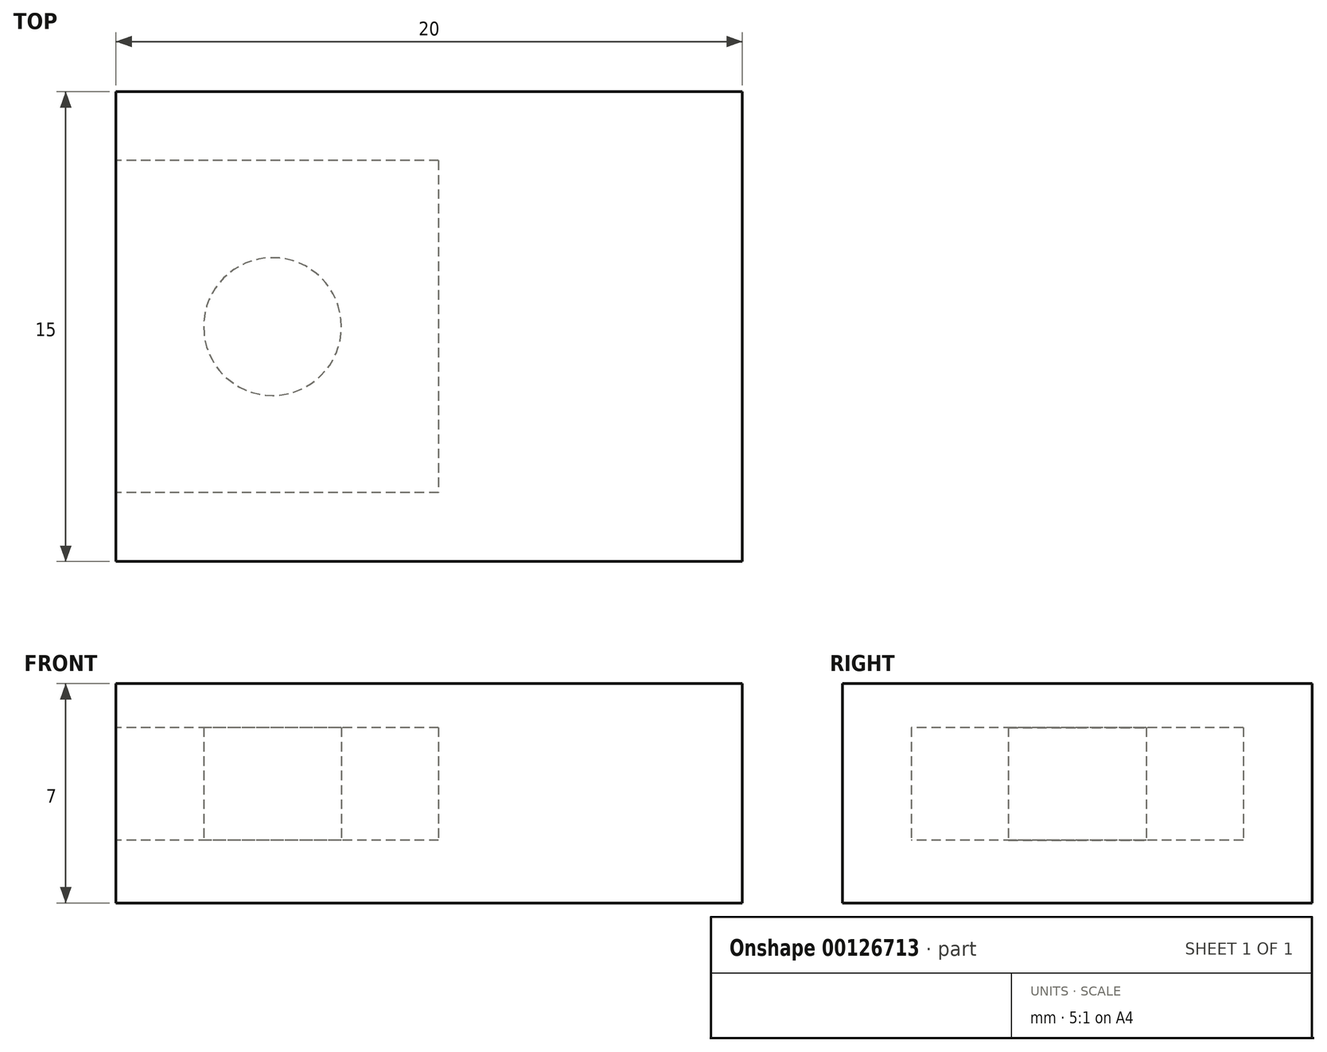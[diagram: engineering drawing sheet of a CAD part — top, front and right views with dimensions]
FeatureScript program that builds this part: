
annotation { "Feature Type Name" : "Feature", "Feature Type Description" : "" }
export const myFeature = defineFeature(function(context is Context, id is Id, definition is map)
    precondition{}
    {
        {
            var Q0;
            Q0=qCreatedBy(makeId("Top.planeOp"),FACE);
            var sketch = newSketch(context, id + "F0", { "sketchPlane" : qUnion([Q0])});
            skLineSegment(sketch, "E0.bottom", {"start": v(-10, 7.5) * mm, "end": v(10, 7.5) * mm});
            skLineSegment(sketch, "E0.top", {"start": v(-10, -7.5) * mm, "end": v(10, -7.5) * mm});
            skLineSegment(sketch, "E0.left", {"start": v(-10, 7.5) * mm, "end": v(-10, -7.5) * mm});
            skLineSegment(sketch, "E0.right", {"start": v(10, 7.5) * mm, "end": v(10, -7.5) * mm});
            skLineSegment(sketch, "E1", {"start": v(-10, -7.5) * mm, "end": v(10, 7.5) * mm, "construction": true});
            skLineSegment(sketch, "E2.bottom", {"start": v(0, 5) * mm, "end": v(-10, 5) * mm, "construction": true});
            skLineSegment(sketch, "E2.top", {"start": v(0, -5) * mm, "end": v(-10, -5) * mm, "construction": true});
            skLineSegment(sketch, "E2.left", {"start": v(0, 5) * mm, "end": v(0, -5) * mm, "construction": true});
            skLineSegment(sketch, "E2.right", {"start": v(-10, 5) * mm, "end": v(-10, -5) * mm, "construction": true});
            skLineSegment(sketch, "E3", {"start": v(0, 5) * mm, "end": v(-10, -5) * mm, "construction": true});
            skCircle(sketch, "E4", {"center": v(-5, 0) * mm, "radius": 2.2 * mm, "construction": true});
            skSolve(sketch);
        }
        {
            var Q0;
            Q0 = qSketchRegion(id + "F0", true);
            extrude(context, id + "F1", {"entities" : qUnion([Q0]), "depth" : 7 * mm});
        }
        {
            var Q0;
            Q0=qCreatedBy(makeId("Top.planeOp"),FACE);
            cPlane(context, id + "F2", {"entities" : qUnion([Q0]), "cplaneType" : CPlaneType.OFFSET, "offset" : 2 * mm, "width" : 150 * mm, "height" : 150 * mm});
        }
        {
            var Q0;
            Q0=qCreatedBy(id+"F2.planeOp",FACE);
            var sketch = newSketch(context, id + "F3", { "sketchPlane" : qUnion([Q0])});
            skLineSegment(sketch, "E5.0", {"start": v(0, 5) * mm, "end": v(-10, 5) * mm, "construction": true});
            skLineSegment(sketch, "E5.1", {"start": v(0, 5) * mm, "end": v(0, -5) * mm, "construction": true});
            skLineSegment(sketch, "E5.2", {"start": v(0, -5) * mm, "end": v(-10, -5) * mm, "construction": true});
            skCircle(sketch, "E5.3", {"center": v(-5, 0) * mm, "radius": 2.2 * mm, "construction": true});
            skLineSegment(sketch, "E5.4", {"start": v(-10, 5) * mm, "end": v(-10, -5) * mm, "construction": true});
            skLineSegment(sketch, "E6.0", {"start": v(-10.3, 5.3) * mm, "end": v(-10.3, -5.3) * mm});
            skLineSegment(sketch, "E6.1", {"start": v(0.3, 5.3) * mm, "end": v(-10.3, 5.3) * mm});
            skLineSegment(sketch, "E6.2", {"start": v(0.3, 5.3) * mm, "end": v(0.3, -5.3) * mm});
            skLineSegment(sketch, "E6.3", {"start": v(0.3, -5.3) * mm, "end": v(-10.3, -5.3) * mm});
            skSolve(sketch);
        }
        {
            var Q0;
            Q0 = qSketchRegion(id + "F3", true);
            var Q1;
            Q1 = qConstructionFilter(qBodyType(qCreatedBy(id + "F3" ,EDGE), BodyType.WIRE), ConstructionObject.NO);
            extrude(context, id + "F4", {"entities" : qUnion([Q0]), "operationType" : NewBodyOperationType.REMOVE, "surfaceEntities" : qUnion([Q1]), "depth" : 3.6 * mm});
        }
        {
            var Q0;
            Q0=qCreatedBy(makeId("Top.planeOp"),FACE);
            var sketch = newSketch(context, id + "F5", { "sketchPlane" : qUnion([Q0])});
            skCircle(sketch, "E7.0", {"center": v(-5, 0) * mm, "radius": 2.2 * mm});
            skSolve(sketch);
        }
        {
            var Q0;
            Q0 = qSketchRegion(id + "F5", true);
            var Q1;
            Q1=makeQuery(id+"F1.opExtrude","CAP_FACE",FACE,{"disambiguationData":[OSD([sQuery(id+"F0.wireOp",EDGE,"E0.bottom"),sQuery(id+"F0.wireOp",EDGE,"E0.top"),sQuery(id+"F0.wireOp",EDGE,"E0.left"),sQuery(id+"F0.wireOp",EDGE,"E0.right")])],"isStart":false});
            extrude(context, id + "F6", {"entities" : qUnion([Q0]), "operationType" : NewBodyOperationType.ADD, "endBound" : BoundingType.UP_TO_SURFACE, "endBoundEntityFace" : qUnion([Q1]), "depth" : 25 * mm});
        }
    });
